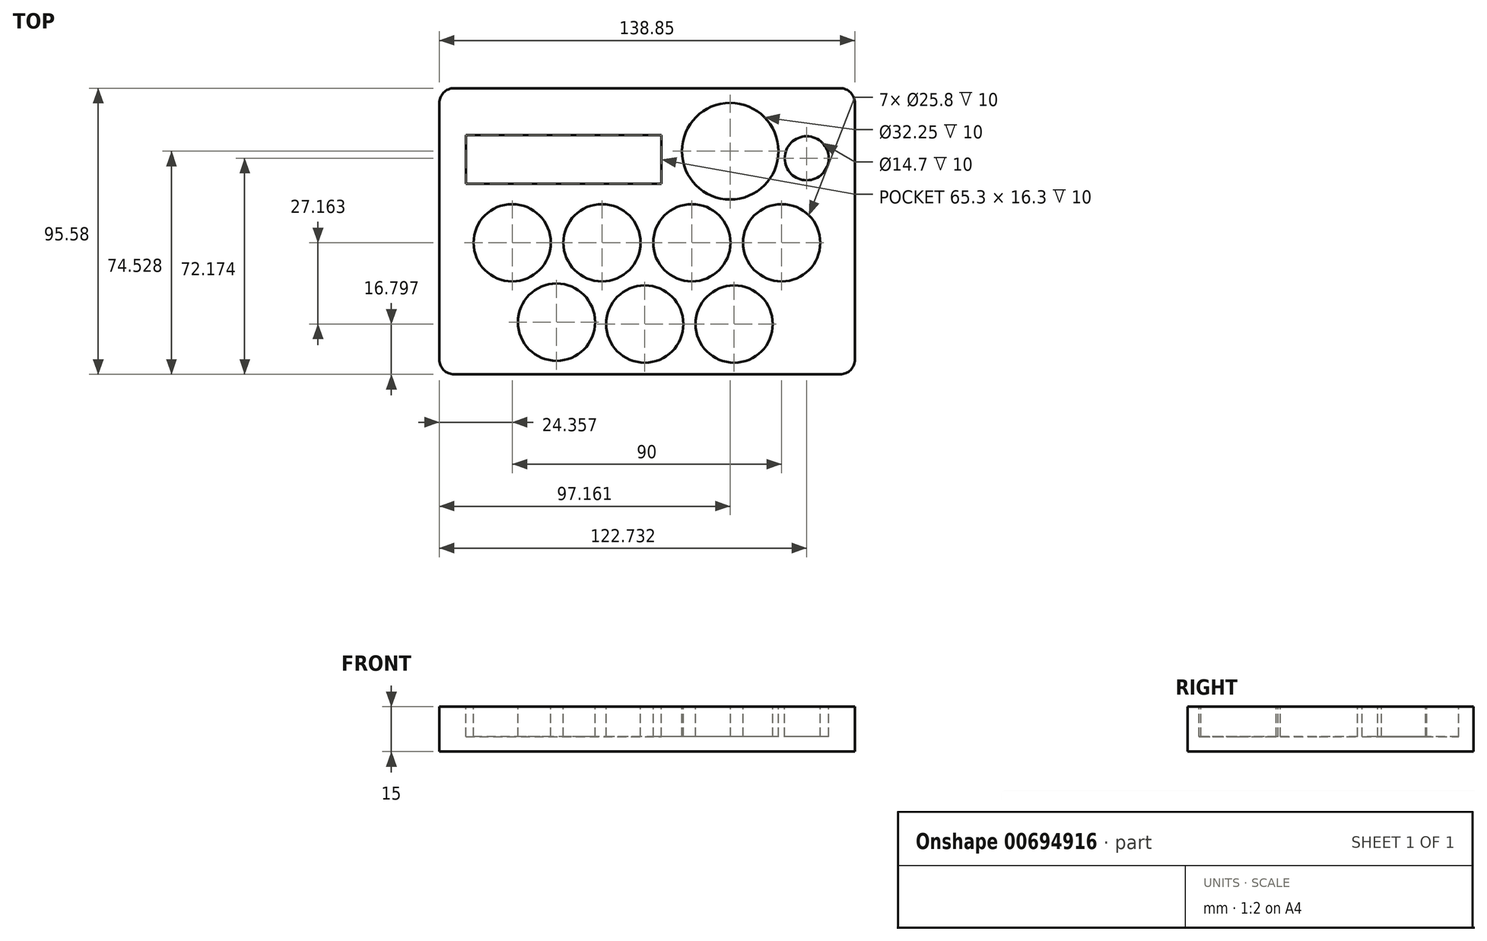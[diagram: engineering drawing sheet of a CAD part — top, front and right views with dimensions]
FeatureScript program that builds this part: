
annotation { "Feature Type Name" : "Feature", "Feature Type Description" : "" }
export const myFeature = defineFeature(function(context is Context, id is Id, definition is map)
    precondition{}
    {
        {
            var Q0;
            Q0=qCreatedBy(makeId("Top.planeOp"),FACE);
            var sketch = newSketch(context, id + "F0", { "sketchPlane" : qUnion([Q0])});
            skCircle(sketch, "E0", {"center": v(-49.9, 0) * mm, "radius": 12.9 * mm, "construction": true});
            skCircle(sketch, "E1.1.0.0", {"center": v(-19.9, 0) * mm, "radius": 12.9 * mm, "construction": true});
            skCircle(sketch, "E2", {"center": v(22.9, 30.57) * mm, "radius": 16.12 * mm, "construction": true});
            skCircle(sketch, "E3", {"center": v(48.47, 28.21) * mm, "radius": 7.35 * mm, "construction": true});
            skCircle(sketch, "E4.1.0.0", {"center": v(-5.63, -27.16) * mm, "radius": 12.9 * mm, "construction": true});
            skCircle(sketch, "E4.1.0.1", {"center": v(24.23, -27.16) * mm, "radius": 12.9 * mm, "construction": true});
            skCircle(sketch, "E5", {"center": v(-35.1, -26.53) * mm, "radius": 12.9 * mm, "construction": true});
            skCircle(sketch, "E6", {"center": v(40.1, 0) * mm, "radius": 12.9 * mm, "construction": true});
            skCircle(sketch, "E7", {"center": v(10.1, 0) * mm, "radius": 12.9 * mm, "construction": true});
            skLineSegment(sketch, "E8.bottom", {"start": v(-65.4, 35.95) * mm, "end": v(-0.1, 35.95) * mm, "construction": true});
            skLineSegment(sketch, "E8.top", {"start": v(-65.4, 19.65) * mm, "end": v(-0.1, 19.65) * mm, "construction": true});
            skLineSegment(sketch, "E8.left", {"start": v(-65.4, 35.95) * mm, "end": v(-65.4, 19.65) * mm, "construction": true});
            skLineSegment(sketch, "E8.right", {"start": v(-0.1, 35.95) * mm, "end": v(-0.1, 19.65) * mm, "construction": true});
            skSolve(sketch);
        }
        {
            var Q0;
            Q0=qCreatedBy(makeId("Top.planeOp"),FACE);
            var sketch = newSketch(context, id + "F1", { "sketchPlane" : qUnion([Q0])});
            skLineSegment(sketch, "E9.bottom", {"start": v(-74.26, 51.62) * mm, "end": v(64.59, 51.62) * mm});
            skLineSegment(sketch, "E9.top", {"start": v(-74.26, -43.96) * mm, "end": v(64.59, -43.96) * mm});
            skLineSegment(sketch, "E9.left", {"start": v(-74.26, 51.62) * mm, "end": v(-74.26, -43.96) * mm});
            skLineSegment(sketch, "E9.right", {"start": v(64.59, 51.62) * mm, "end": v(64.59, -43.96) * mm});
            skSolve(sketch);
        }
        {
            var Q0;
            Q0 = qSketchRegion(id + "F1", true);
            extrude(context, id + "F2", {"entities" : qUnion([Q0]), "depth" : 15 * mm, "offsetDistance" : 25 * mm});
        }
        {
            var Q0;
            Q0=makeQuery(id+"F2.opExtrude","CAP_FACE",FACE,{"disambiguationData":[OSD([sQuery(id+"F1.wireOp",EDGE,"E9.bottom"),sQuery(id+"F1.wireOp",EDGE,"E9.top"),sQuery(id+"F1.wireOp",EDGE,"E9.left"),sQuery(id+"F1.wireOp",EDGE,"E9.right")])],"isStart":false});
            var sketch = newSketch(context, id + "F3", { "sketchPlane" : qUnion([Q0])});
            skCircle(sketch, "E10.0", {"center": v(10.1, 0) * mm, "radius": 12.9 * mm});
            skLineSegment(sketch, "E10.1", {"start": v(-65.4, 19.65) * mm, "end": v(-0.1, 19.65) * mm});
            skCircle(sketch, "E10.2", {"center": v(-19.9, 0) * mm, "radius": 12.9 * mm});
            skLineSegment(sketch, "E10.3", {"start": v(-65.4, 35.95) * mm, "end": v(-0.1, 35.95) * mm});
            skLineSegment(sketch, "E10.4", {"start": v(-0.1, 35.95) * mm, "end": v(-0.1, 19.65) * mm});
            skCircle(sketch, "E10.5", {"center": v(40.1, 0) * mm, "radius": 12.9 * mm});
            skCircle(sketch, "E10.6", {"center": v(-49.9, 0) * mm, "radius": 12.9 * mm});
            skLineSegment(sketch, "E10.7", {"start": v(-65.4, 35.95) * mm, "end": v(-65.4, 19.65) * mm});
            skCircle(sketch, "E10.8", {"center": v(48.47, 28.21) * mm, "radius": 7.35 * mm});
            skCircle(sketch, "E10.9", {"center": v(-5.63, -27.16) * mm, "radius": 12.9 * mm});
            skCircle(sketch, "E10.10", {"center": v(-35.1, -26.53) * mm, "radius": 12.9 * mm});
            skCircle(sketch, "E10.11", {"center": v(22.9, 30.57) * mm, "radius": 16.12 * mm});
            skCircle(sketch, "E10.12", {"center": v(24.23, -27.16) * mm, "radius": 12.9 * mm});
            skSolve(sketch);
        }
        {
            var Q0;
            Q0 = qSketchRegion(id + "F3", true);
            extrude(context, id + "F4", {"entities" : qUnion([Q0]), "operationType" : NewBodyOperationType.REMOVE, "oppositeDirection" : true, "depth" : 10 * mm, "offsetDistance" : 25 * mm});
        }
        {
            var Q0;
            Q0=makeQuery(id+"F2.opExtrude","SWEPT_EDGE",EDGE,{"disambiguationData":[OSD([sQuery(id+"F1.wireOp",EDGE,"E9.top"),sQuery(id+"F1.wireOp",EDGE,"E9.right")])]});
            var Q1;
            Q1=makeQuery(id+"F2.opExtrude","SWEPT_EDGE",EDGE,{"disambiguationData":[OSD([sQuery(id+"F1.wireOp",EDGE,"E9.top"),sQuery(id+"F1.wireOp",EDGE,"E9.left")])]});
            var Q2;
            Q2=makeQuery(id+"F2.opExtrude","SWEPT_EDGE",EDGE,{"disambiguationData":[OSD([sQuery(id+"F1.wireOp",EDGE,"E9.bottom"),sQuery(id+"F1.wireOp",EDGE,"E9.right")])]});
            var Q3;
            Q3=makeQuery(id+"F2.opExtrude","SWEPT_EDGE",EDGE,{"disambiguationData":[OSD([sQuery(id+"F1.wireOp",EDGE,"E9.bottom"),sQuery(id+"F1.wireOp",EDGE,"E9.left")])]});
            fillet(context, id + "F5", {"entities" : qUnion([Q0, Q1, Q2, Q3]), "radius" : 5 * mm, "tangentPropagation" : true, "allowEdgeOverflow" : false});
        }
    });
